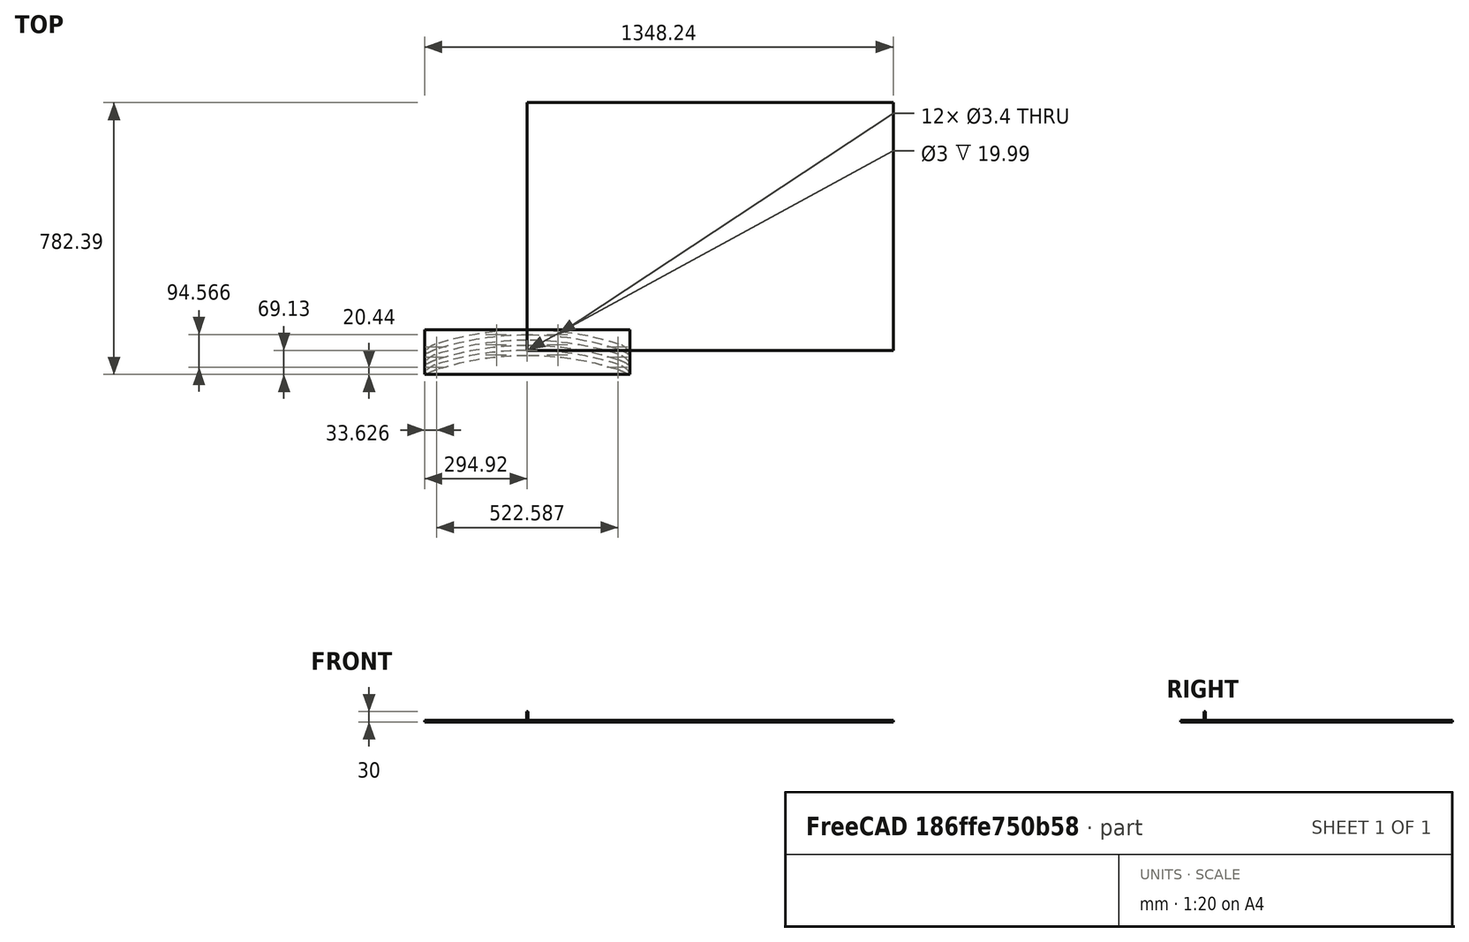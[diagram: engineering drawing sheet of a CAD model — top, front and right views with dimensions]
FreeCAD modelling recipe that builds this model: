
FCSTD DOCUMENT  (FreeCAD 0.21R32532 (Git))
Label: composit_full_size_PP_milling
License: All rights reserved
LicenseURL: http://en.wikipedia.org/wiki/All_rights_reserved
objects: Part::FeaturePython×10, Path::FeaturePython×8, App::DocumentObjectGroup×6, App::Link×4, App::FeaturePython×2
note: 13 computed .brp shape members not serialized (recipe doc carries the construction recipe); baked Part::Feature solids carry a one-line shape summary decoded from their .brp
EXTERNAL_REF file=composit_full_size2part.FCStd obj=Body019
EXTERNAL_REF file=composit_full_size2part.FCStd obj=Body042
EXTERNAL_REF file=composit_full_size2part.FCStd obj=Body022
EXTERNAL_REF file=composit_full_size2part.FCStd obj=Body013

FEATURE [App::Link] Link
  LinkedObject = -> <external composit_full_size2part.FCStd>#Body019
  expr: LinkedObject = <<composit_full_size2part>>#<<basement_proxy>>._self
FEATURE [App::Link] Link001
  LinkedObject = -> <external composit_full_size2part.FCStd>#Body042
  expr: LinkedObject = <<composit_full_size2part>>#<<basement2_proxy>>._self
FEATURE [App::Link] Link002
  LinkedObject = -> <external composit_full_size2part.FCStd>#Body022
  expr: LinkedObject = <<composit_full_size2part>>#<<basin_limiter_body>>._self
FEATURE [App::FeaturePython] SetupSheet  # Path/CAM operation (typed FeaturePython)
  ClearanceHeightExpression = OpStockZMax+SetupSheet.ClearanceHeightOffset
  ClearanceHeightOffset = 5
  CoolantMode = 0
  CoolantModes = None | Flood | Mist
  FinalDepthExpression = -0.1 mm
  HorizRapid = 0
  ProfileDirection = 1
  ProfileSide = 0
  ProfileUseComp = true
  ProfileprocessCircles = true
  ProfileprocessHoles = true
  ProfileprocessPerimeter = true
  SafeHeightExpression = OpStockZMax+SetupSheet.SafeHeightOffset
  SafeHeightOffset = 3
  StartDepthExpression = 3 mm
  StepDownExpression = 4 mm
  VertRapid = 0
FEATURE [Part::FeaturePython] Clone  label="Model-Link"  # Draft clone (typed FeaturePython)
  AttacherType = Attacher::AttachEngine3D
  Fuse = false
  Objects = -> [Link]
  PathResource = Model
  Placement = pos=(732.67,453.26,0) rot=(0,0,1;0rad)
  Scale = (1,1,1)
FEATURE [Part::FeaturePython] Clone001  label="Model-Link001"  # Draft clone (typed FeaturePython)
  AttacherType = Attacher::AttachEngine3D
  Fuse = false
  Objects = -> [Link001]
  PathResource = Model
  Placement = pos=(347.67,228.26,0) rot=(0,0,1;0rad)
  Scale = (1,1,1)
FEATURE [Part::FeaturePython] Clone002  label="Model-Link002"  # Draft clone (typed FeaturePython)
  AttacherType = Attacher::AttachEngine3D
  Fuse = false
  Objects = -> [Link002]
  PathResource = Model
  Placement = pos=(-0.0995012,363.984,2.866e-13) rot=(0,0,1;4.18879rad)
  Scale = (1,1,1)
FEATURE [App::DocumentObjectGroup] Model
  Group = -> [Clone,Clone001,Clone002]
FEATURE [Part::FeaturePython] ToolBit  label="3.175mm Endmill"  # Path/CAM toolbit (typed FeaturePython)
  BitPropertyNames = Chipload | CuttingEdgeHeight | Diameter | Flutes | Length | Material | ShankDiameter | SpindleDirection
  BitShape = <path>
  Chipload = 0
  CuttingEdgeHeight = 30
  Diameter = 3.17
  Flutes = 0
  Length = 10
  Material = 0
  ShankDiameter = 3
  ShapeName = endmill
  SpindleDirection = 0
FEATURE [Path::FeaturePython] __175mm_Endmill  label="3.175mm Endmill001"  # Path/CAM operation (typed FeaturePython)
  HorizFeed = 33.3333
  HorizRapid = 0
  SpindleDir = 0
  SpindleSpeed = 18000
  Tool = -> ToolBit
  ToolNumber = 1
  VertFeed = 8.33333
  VertRapid = 0
  expr: HorizRapid = SetupSheet.HorizRapid
  expr: VertRapid = SetupSheet.VertRapid
FEATURE [App::DocumentObjectGroup] Tools
  Group = -> [__175mm_Endmill]
FEATURE [Part::FeaturePython] Stock001  # WARN: FeaturePython — macro-defined, semantics opaque (R4)
  Base = -> Model
  ExtXneg = 0
  ExtXpos = 1
  ExtYneg = 0
  ExtYpos = 1
  ExtZneg = 0
  ExtZpos = 1
  StockType = FromBase
FEATURE [Path::FeaturePython] Profile  # Path/CAM operation (typed FeaturePython)
  Active = true
  AreaParams:
    Tolerance = 1e-07
    FitArcs = True
    Simplify = False
    CleanDistance = 0.0
    Accuracy = 0.01
    Unit = 1.0
    MinArcPoints = 4
    MaxArcPoints = 100
    ClipperScale = 10000000.0
    Fill = 0
    Coplanar = 0
    Reorient = True
    Outline = False
    Explode = False
    OpenMode = 0
    Deflection = 0.01
    SubjectFill = 0
    ClipFill = 0
    Offset = -1.585
    ExtraPass = 0
    Stepover = 0.0
    LastStepover = 0.0
    JoinType = 0
    EndType = 0
    MiterLimit = 2.0
    RoundPrecision = 0.0
    PocketMode = 0
    ToolRadius = 1.0
    PocketExtraOffset = 0.0
    PocketStepover = 0.0
    PocketLastStepover = 0.0
    FromCenter = False
    Angle = 45.0
    AngleShift = 0.0
    Shift = 0.0
    Thicken = False
    SectionCount = -1
    Stepdown = 1.0
    SectionOffset = 0.0
    SectionTolerance = 1e-07
    SectionMode = 2
    Project = False
  Base = -> [Clone002,Clone001,Clone]
  ClearanceHeight = 9
  CoolantMode = 0
  CycleTime = 00:03:54
  Direction = 1
  FinalDepth = -0.1
  HandleMultipleFeatures = 0
  JoinType = 0
  MiterLimit = 0.1
  OffsetExtra = 0
  OpFinalDepth = 0
  OpStartDepth = 4
  OpStockZMax = 4
  OpStockZMin = 0
  OpToolDiameter = 3.17
  PathParams = {'orientation': 1, 'feedrate': 33.333333333333336, 'feedrate_v': 8.333333333333334, 'verbose': True, 'resume_height': 7.000000000000657, 'retraction': 9.000000000000657, 'return_end': True, 'preamble': False, 'start': Vector (379.5856753098799, 193.78742219435313, 9.000000000000657)}
  SafeHeight = 7
  Side = 0
  SplitArcs = false
  StartDepth = 3
  StartPoint = (0,0,0)
  StepDown = 4
  ToolController = -> __175mm_Endmill
  UseComp = true
  UseStartPoint = false
  processCircles = true
  processHoles = true
  processPerimeter = false
  expr: ClearanceHeight = OpStockZMax + SetupSheet.ClearanceHeightOffset
  expr: FinalDepth = -0.1 mm
  expr: SafeHeight = OpStockZMax + SetupSheet.SafeHeightOffset
  expr: StartDepth = 3 mm
  expr: StepDown = 4 mm
FEATURE [Path::FeaturePython] Profile001  # Path/CAM operation (typed FeaturePython)
  Active = true
  AreaParams:
    Tolerance = 1e-07
    FitArcs = True
    Simplify = False
    CleanDistance = 0.0
    Accuracy = 0.01
    Unit = 1.0
    MinArcPoints = 4
    MaxArcPoints = 100
    ClipperScale = 10000000.0
    Fill = 0
    Coplanar = 0
    Reorient = True
    Outline = False
    Explode = False
    OpenMode = 0
    Deflection = 0.01
    SubjectFill = 0
    ClipFill = 0
    Offset = 1.585
    ExtraPass = 0
    Stepover = 0.0
    LastStepover = 0.0
    JoinType = 0
    EndType = 0
    MiterLimit = 2.0
    RoundPrecision = 0.0
    PocketMode = 0
    ToolRadius = 1.0
    PocketExtraOffset = 0.0
    PocketStepover = 0.0
    PocketLastStepover = 0.0
    FromCenter = False
    Angle = 45.0
    AngleShift = 0.0
    Shift = 0.0
    Thicken = False
    SectionCount = -1
    Stepdown = 1.0
    SectionOffset = 0.0
    SectionTolerance = 1e-07
    SectionMode = 2
    Project = False
  ClearanceHeight = 9
  CoolantMode = 0
  CycleTime = 00:02:38
  Direction = 1
  FinalDepth = -0.1
  HandleMultipleFeatures = 0
  JoinType = 0
  MiterLimit = 0.1
  OffsetExtra = 0
  OpFinalDepth = 0
  OpStartDepth = 4
  OpStockZMax = 4
  OpStockZMin = 0
  OpToolDiameter = 3.17
  PathParams = {'orientation': 0, 'feedrate': 33.333333333333336, 'feedrate_v': 8.333333333333334, 'verbose': True, 'resume_height': 7.000000000000657, 'retraction': 9.000000000000657, 'return_end': True, 'preamble': False, 'start': Vector (244.67692648785436, 419.0655834400178, 9.000000000000657)}
  SafeHeight = 7
  Side = 0
  SplitArcs = false
  StartDepth = 3
  StartPoint = (0,0,0)
  StepDown = 4
  ToolController = -> __175mm_Endmill
  UseComp = true
  UseStartPoint = false
  processCircles = true
  processHoles = true
  processPerimeter = true
  expr: ClearanceHeight = OpStockZMax + SetupSheet.ClearanceHeightOffset
  expr: FinalDepth = -0.1 mm
  expr: SafeHeight = OpStockZMax + SetupSheet.SafeHeightOffset
  expr: StartDepth = 3 mm
  expr: StepDown = 4 mm
FEATURE [App::DocumentObjectGroup] Operations
  Group = -> [Profile,Profile001]
FEATURE [Path::FeaturePython] Job  # Path/CAM operation (typed FeaturePython)
  CycleTime = 00:06:32
  Fixtures = G54
  GeometryTolerance = 0.01
  JobType = 0
  LastPostProcessDate = 2023-03-28 13:09:00.568011
  LastPostProcessOutput = <userpath>/56D3-E9D0/Job-0.tap \n<userpath>/56D3-E9D0/Job-1.tap
  Model = -> Model
  Operations = -> Operations
  OrderOutputBy = 2
  PostProcessor = 1
  PostProcessorOutputFile = %d.%j.tap
  SetupSheet = -> SetupSheet
  SplitOutput = true
  Stock = -> Stock001
  Tools = -> Tools
FEATURE [App::Link] Link003
  LinkedObject = -> <external composit_full_size2part.FCStd>#Body013
  expr: LinkedObject = <<composit_full_size2part>>#<<Body013>>._self
FEATURE [App::FeaturePython] SetupSheet001  # Path/CAM operation (typed FeaturePython)
  ClearanceHeightExpression = OpStockZMax+SetupSheet001.ClearanceHeightOffset
  ClearanceHeightOffset = 5
  CoolantMode = 0
  CoolantModes = None | Flood | Mist
  FinalDepthExpression = -0.1 mm
  HorizRapid = 0
  ProfileDirection = 1
  ProfileSide = 0
  ProfileUseComp = true
  ProfileprocessCircles = true
  ProfileprocessHoles = true
  ProfileprocessPerimeter = true
  SafeHeightExpression = OpStockZMax+SetupSheet001.SafeHeightOffset
  SafeHeightOffset = 3
  StartDepthExpression = 3 mm
  StepDownExpression = 4 mm
  VertRapid = 0
FEATURE [Part::FeaturePython] Clone003  label="Model-Link003"  # Draft clone (typed FeaturePython)
  AttacherType = Attacher::AttachEngine3D
  Fuse = false
  Objects = -> [Link003]
  PathResource = Model
  Placement = pos=(0,-242,0) rot=(0,0,1;0rad)
  Scale = (1,1,1)
FEATURE [Part::FeaturePython] Clone004  label="Model-Link004"  # Draft clone (typed FeaturePython)
  AttacherType = Attacher::AttachEngine3D
  AttachmentOffset = pos=(0,0,5) rot=(0,0,1;0rad)
  Fuse = false
  Objects = -> [Link003]
  PathResource = Model
  Placement = pos=(0,-213,0) rot=(0,0,1;0rad)
  Scale = (1,1,1)
FEATURE [Part::FeaturePython] Clone005  label="Model-Link005"  # Draft clone (typed FeaturePython)
  AttacherType = Attacher::AttachEngine3D
  Fuse = false
  Objects = -> [Link003]
  PathResource = Model
  Placement = pos=(0,-183,0) rot=(0,0,1;0rad)
  Scale = (1,1,1)
FEATURE [App::DocumentObjectGroup] Model001
  Group = -> [Clone003,Clone004,Clone005]
FEATURE [Part::FeaturePython] ToolBit001  label="3.175mm Endmill003"  # Path/CAM toolbit (typed FeaturePython)
  BitPropertyNames = Chipload | CuttingEdgeHeight | Diameter | Flutes | Length | Material | ShankDiameter | SpindleDirection
  BitShape = <path>
  Chipload = 0
  CuttingEdgeHeight = 30
  Diameter = 3.17
  Flutes = 0
  Length = 10
  Material = 0
  ShankDiameter = 3
  ShapeName = endmill
  SpindleDirection = 0
FEATURE [Path::FeaturePython] __175mm_Endmill001  label="3.175mm Endmill002"  # Path/CAM operation (typed FeaturePython)
  HorizFeed = 33.3333
  HorizRapid = 0
  SpindleDir = 0
  SpindleSpeed = 18000
  Tool = -> ToolBit001
  ToolNumber = 1
  VertFeed = 8.33333
  VertRapid = 0
  expr: HorizRapid = SetupSheet001.HorizRapid
  expr: VertRapid = SetupSheet001.VertRapid
FEATURE [App::DocumentObjectGroup] Tools001
  Group = -> [__175mm_Endmill001]
FEATURE [Part::FeaturePython] Stock  # WARN: FeaturePython — macro-defined, semantics opaque (R4)
  Base = -> Model001
  ExtXneg = 1
  ExtXpos = 1
  ExtYneg = 1
  ExtYpos = 0
  ExtZneg = 0
  ExtZpos = 1
  Placement = pos=(-293.924,-68.126,-3.6e-15) rot=(0,0,1;0rad)
  StockType = FromBase
FEATURE [Path::FeaturePython] Profile002  # Path/CAM operation (typed FeaturePython)
  Active = true
  AreaParams:
    Tolerance = 1e-07
    FitArcs = True
    Simplify = False
    CleanDistance = 0.0
    Accuracy = 0.01
    Unit = 1.0
    MinArcPoints = 4
    MaxArcPoints = 100
    ClipperScale = 10000000.0
    Fill = 0
    Coplanar = 0
    Reorient = True
    Outline = False
    Explode = False
    OpenMode = 0
    Deflection = 0.01
    SubjectFill = 0
    ClipFill = 0
    Offset = 1.585
    ExtraPass = 0
    Stepover = 0.0
    LastStepover = 0.0
    JoinType = 0
    EndType = 0
    MiterLimit = 2.0
    RoundPrecision = 0.0
    PocketMode = 0
    ToolRadius = 1.0
    PocketExtraOffset = 0.0
    PocketStepover = 0.0
    PocketLastStepover = 0.0
    FromCenter = False
    Angle = 45.0
    AngleShift = 0.0
    Shift = 0.0
    Thicken = False
    SectionCount = -1
    Stepdown = 1.0
    SectionOffset = 0.0
    SectionTolerance = 1e-07
    SectionMode = 2
    Project = False
  ClearanceHeight = 9
  CoolantMode = 0
  CycleTime = 00:02:07
  Direction = 1
  FinalDepth = -0.1
  HandleMultipleFeatures = 0
  JoinType = 0
  MiterLimit = 0.1
  OffsetExtra = 0
  OpFinalDepth = -3.6e-15
  OpStartDepth = 4
  OpStockZMax = 4
  OpStockZMin = -3.6e-15
  OpToolDiameter = 3.17
  PathParams = {'orientation': 0, 'feedrate': 33.333333333333336, 'feedrate_v': 8.333333333333334, 'verbose': True, 'resume_height': 7.000000000000007, 'retraction': 9.000000000000007, 'return_end': True, 'preamble': False, 'start': Vector (-289.20758563762087, -40.67626583107504, 9.000000000000007)}
  SafeHeight = 7
  Side = 0
  SplitArcs = false
  StartDepth = 3
  StartPoint = (-290,-60,0)
  StepDown = 4
  ToolController = -> __175mm_Endmill001
  UseComp = true
  UseStartPoint = true
  processCircles = true
  processHoles = true
  processPerimeter = true
  expr: ClearanceHeight = OpStockZMax + SetupSheet001.ClearanceHeightOffset
  expr: FinalDepth = -0.1 mm
  expr: SafeHeight = OpStockZMax + SetupSheet001.SafeHeightOffset
  expr: StartDepth = 3 mm
  expr: StepDown = 4 mm
FEATURE [Path::FeaturePython] DressupTag  # Path/CAM operation (typed FeaturePython)
  Angle = 45
  Base = -> Profile002
  Height = 1.5
  Positions = (3) [(-272.43,-42.64,0),(-273.47,-14.16,0),(-276.83,13.98,0)]
  Radius = 0
  SegmentationFactor = 50
  Width = 10
FEATURE [App::DocumentObjectGroup] Operations001
  Group = -> [DressupTag]
FEATURE [Path::FeaturePython] Job001  # Path/CAM operation (typed FeaturePython)
  CycleTime = 00:02:07
  Fixtures = G54
  GeometryTolerance = 0.01
  JobType = 0
  LastPostProcessDate = 2023-03-28 15:41:56.815475
  LastPostProcessOutput = <userpath>/56D3-E9D0/Job.tap
  Model = -> Model001
  Operations = -> Operations001
  OrderOutputBy = 0
  PostProcessor = 1
  PostProcessorOutputFile = %d.%j.tap
  SetupSheet = -> SetupSheet001
  SplitOutput = false
  Stock = -> Stock
  Tools = -> Tools001
note: 2 file-system paths scrubbed to <path> (originals preserved in the JSON sidecar)
